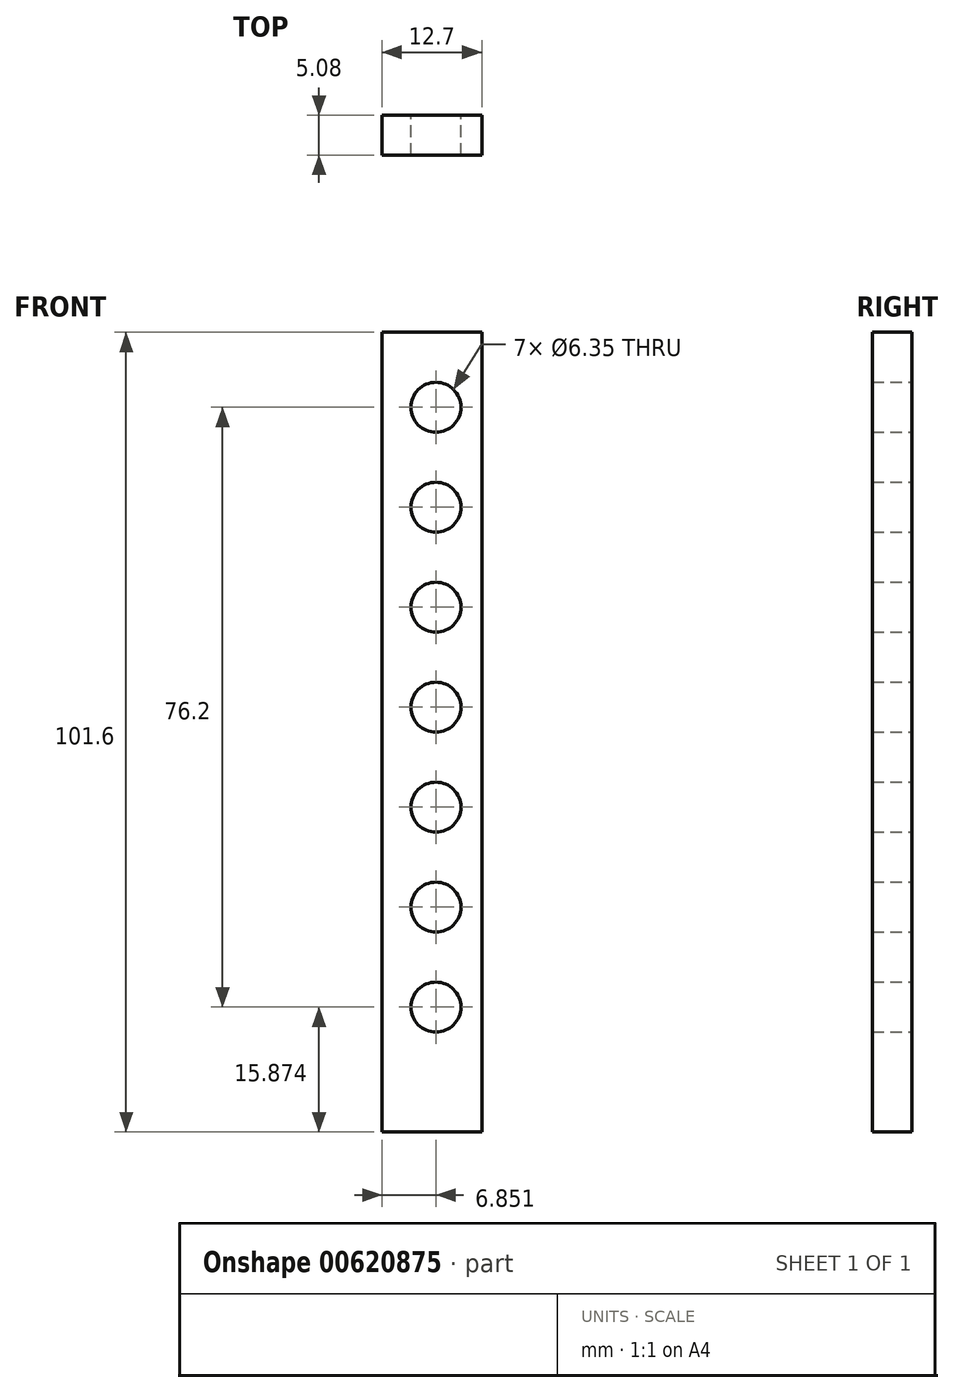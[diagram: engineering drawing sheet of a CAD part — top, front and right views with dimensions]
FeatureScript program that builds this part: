
annotation { "Feature Type Name" : "Feature", "Feature Type Description" : "" }
export const myFeature = defineFeature(function(context is Context, id is Id, definition is map)
    precondition{}
    {
        {
            var Q0;
            Q0=qCreatedBy(makeId("Front.planeOp"),FACE);
            var sketch = newSketch(context, id + "F0", { "sketchPlane" : qUnion([Q0])});
            skLineSegment(sketch, "E0.bottom", {"start": v(-9.43, 47.4) * mm, "end": v(3.27, 47.4) * mm});
            skLineSegment(sketch, "E0.top", {"start": v(-9.43, -54.2) * mm, "end": v(3.27, -54.2) * mm});
            skLineSegment(sketch, "E0.left", {"start": v(-9.43, 47.4) * mm, "end": v(-9.43, -54.2) * mm});
            skLineSegment(sketch, "E0.right", {"start": v(3.27, 47.4) * mm, "end": v(3.27, -54.2) * mm});
            skLineSegment(sketch, "E1", {"start": v(-2.54, 45.7) * mm, "end": v(-3.08, -54.2) * mm, "construction": true});
            skCircle(sketch, "E2", {"center": v(-2.58, 37.88) * mm, "radius": 3.18 * mm});
            skCircle(sketch, "E3.0.1.0", {"center": v(-2.58, 25.18) * mm, "radius": 3.18 * mm});
            skCircle(sketch, "E3.0.2.0", {"center": v(-2.58, 12.48) * mm, "radius": 3.18 * mm});
            skCircle(sketch, "E3.0.3.0", {"center": v(-2.58, -0.22) * mm, "radius": 3.18 * mm});
            skLineSegment(sketch, "E3.direction1", {"start": v(-2.58, 37.88) * mm, "end": v(22.82, 37.88) * mm, "construction": true});
            skLineSegment(sketch, "E3.direction2", {"start": v(-2.58, 37.88) * mm, "end": v(-2.58, 25.18) * mm, "construction": true});
            skCircle(sketch, "E4.0.0.4", {"center": v(-2.58, -12.92) * mm, "radius": 3.18 * mm});
            skCircle(sketch, "E5.0.0.5", {"center": v(-2.58, -25.62) * mm, "radius": 3.18 * mm});
            skCircle(sketch, "E5.0.0.6", {"center": v(-2.58, -38.32) * mm, "radius": 3.18 * mm});
            skSolve(sketch);
        }
        {
            var Q0;
            Q0 = qSketchRegion(id + "F0", true);
            extrude(context, id + "F1", {"entities" : qUnion([Q0]), "depth" : 5.08 * mm, "offsetDistance" : 25.4 * mm});
        }
    });
